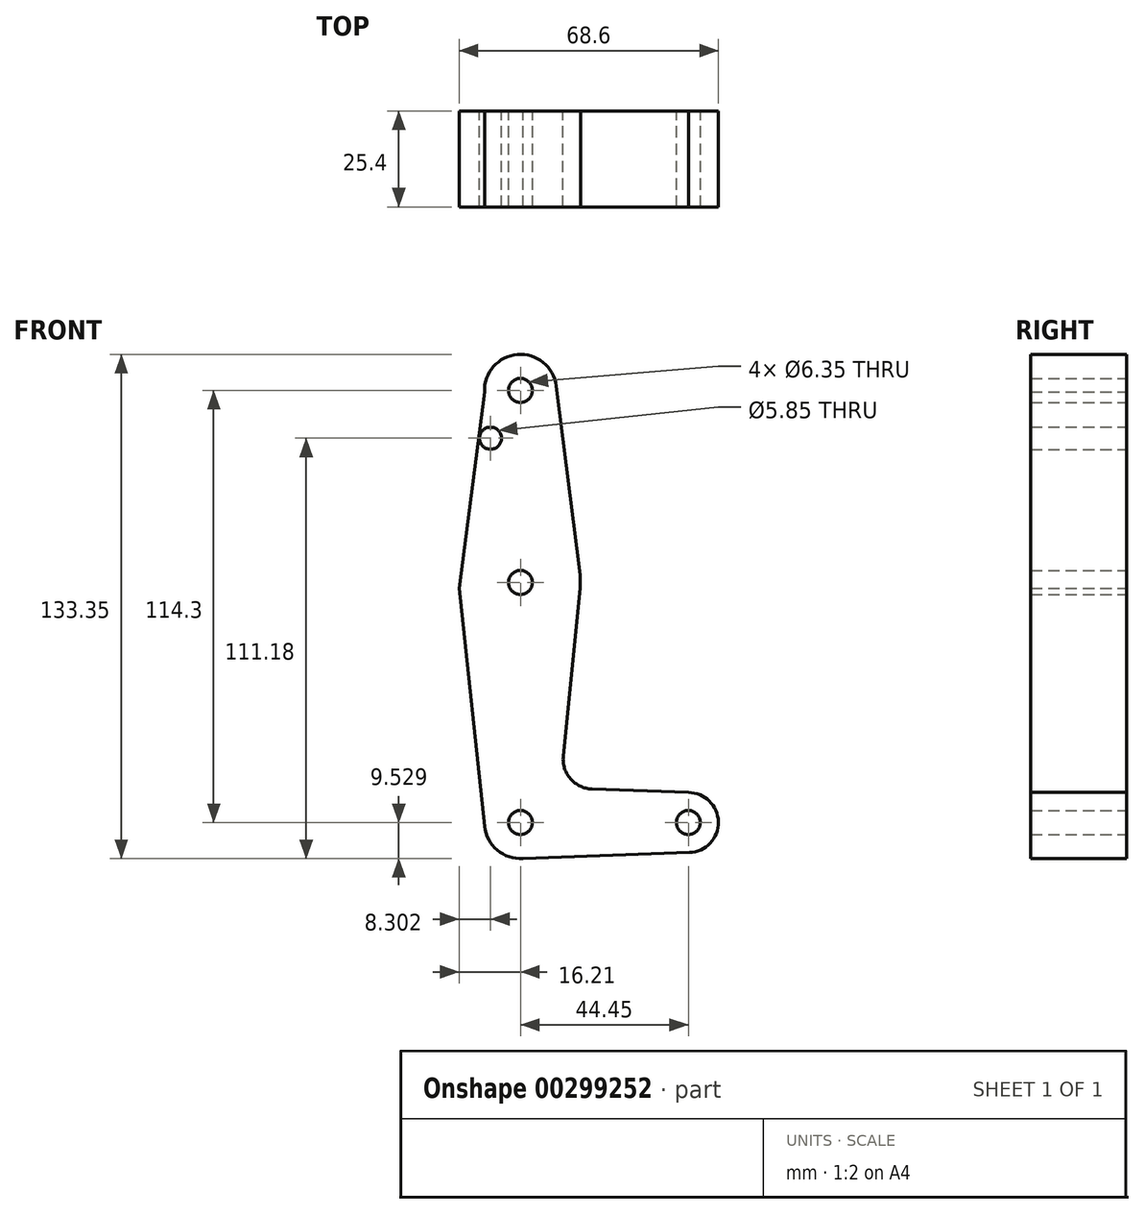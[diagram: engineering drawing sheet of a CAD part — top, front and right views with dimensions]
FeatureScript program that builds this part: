
annotation { "Feature Type Name" : "Feature", "Feature Type Description" : "" }
export const myFeature = defineFeature(function(context is Context, id is Id, definition is map)
    precondition{}
    {
        {
            var Q0;
            Q0=qCreatedBy(makeId("Front.planeOp"),FACE);
            var sketch = newSketch(context, id + "F0", { "sketchPlane" : qUnion([Q0])});
            skLineSegment(sketch, "E0", {"start": v(0, 90.05) * mm, "end": v(0, 39.25) * mm});
            skLineSegment(sketch, "E1", {"start": v(0, 39.25) * mm, "end": v(0, -24.25) * mm});
            skLineSegment(sketch, "E2", {"start": v(0, -24.25) * mm, "end": v(44.45, -24.25) * mm});
            skCircle(sketch, "E3", {"center": v(0, 90.05) * mm, "radius": 9.53 * mm});
            skCircle(sketch, "E4", {"center": v(0, 39.25) * mm, "radius": 15.88 * mm});
            skCircle(sketch, "E5", {"center": v(0, -24.25) * mm, "radius": 9.53 * mm});
            skCircle(sketch, "E6", {"center": v(44.45, -24.25) * mm, "radius": 7.94 * mm});
            skLineSegment(sketch, "E7", {"start": v(9.45, 91.24) * mm, "end": v(15.75, 41.23) * mm});
            skLineSegment(sketch, "E8", {"start": v(15.8, 37.66) * mm, "end": v(11.34, -6.66) * mm});
            skLineSegment(sketch, "E9", {"start": v(18.97, -15.4) * mm, "end": v(44.45, -16.31) * mm});
            skLineSegment(sketch, "E10", {"start": v(0, -33.78) * mm, "end": v(44.73, -32.18) * mm});
            skArc(sketch, "E11.filletArc", {"start": v(11.34, -6.66) * mm, "mid": v(13.26, -12.69) * mm, "end": v(18.97, -15.4) * mm});
            skCircle(sketch, "E12", {"center": v(0, 90.05) * mm, "radius": 3.18 * mm});
            skCircle(sketch, "E13", {"center": v(-7.9, 77.4) * mm, "radius": 2.92 * mm});
            skCircle(sketch, "E14", {"center": v(0, 39.25) * mm, "radius": 3.18 * mm});
            skCircle(sketch, "E15", {"center": v(0, -24.25) * mm, "radius": 3.18 * mm});
            skCircle(sketch, "E16", {"center": v(44.45, -24.25) * mm, "radius": 3.18 * mm});
            skLineSegment(sketch, "E17", {"start": v(-9.52, 89.67) * mm, "end": v(-16.2, 37.68) * mm});
            skLineSegment(sketch, "E18", {"start": v(-16.2, 37.68) * mm, "end": v(-9.47, -25.26) * mm});
            skSolve(sketch);
        }
        {
            var Q0;
            Q0 = qSketchRegion(id + "F0", true);
            var Q1;
            {var subQ0=sQuery(id+"F0.wireOp",EDGE,"E5");var subQ1=sQuery(id+"F0.wireOp",EDGE,"E1");var subQ2=makeQuery(id+"F0.imprint","INTERSECT",VERTEX,{"derivedFrom":[subQ1,subQ0]});Q1=makeQuery(id+"F0.imprint","IMPRINT",FACE,{"disambiguationData":[TD([[makeQuery(id+"F0.imprint","IMPRINT",EDGE,{"disambiguationData":[TD([[subQ2,-1.0]])],"derivedFrom":subQ1}),1.0]])]});}
            extrude(context, id + "F1", {"entities" : qUnion([Q0, Q1]), "depth" : 25.4 * mm});
        }
    });
